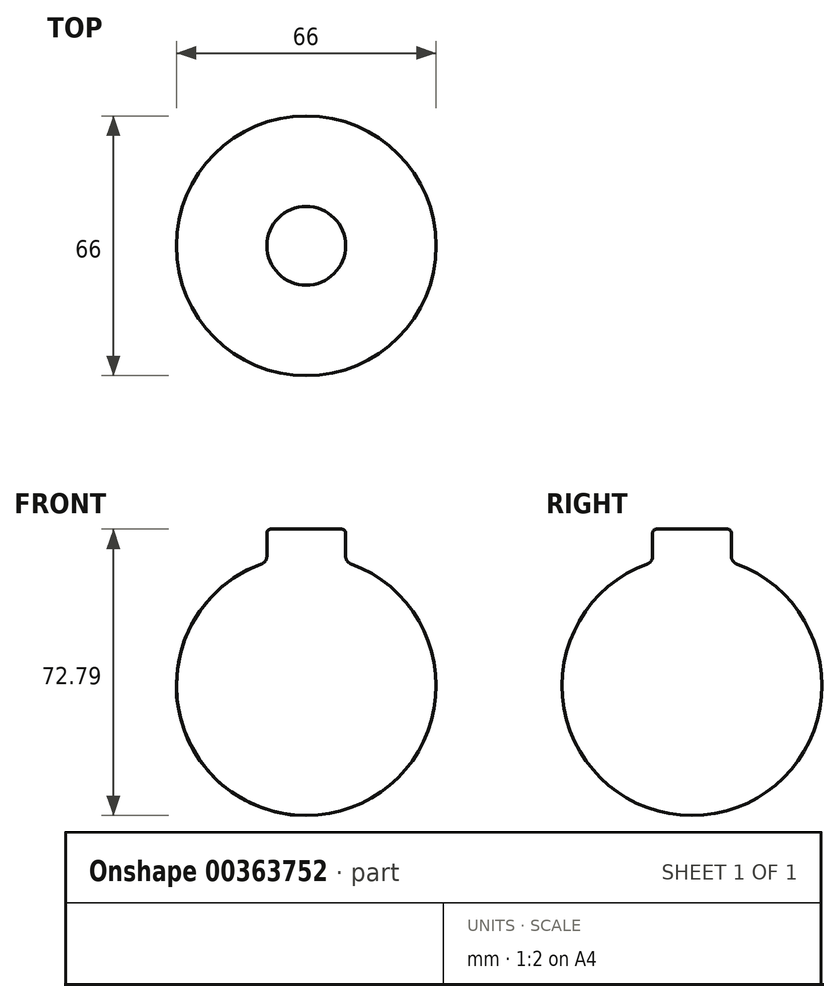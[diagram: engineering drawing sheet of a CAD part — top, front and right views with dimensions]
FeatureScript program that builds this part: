
annotation { "Feature Type Name" : "Feature", "Feature Type Description" : "" }
export const myFeature = defineFeature(function(context is Context, id is Id, definition is map)
    precondition{}
    {
        {
            var Q0;
            Q0=qCreatedBy(makeId("Front.planeOp"),FACE);
            var sketch = newSketch(context, id + "F0", { "sketchPlane" : qUnion([Q0])});
            skCircle(sketch, "E0", {"center": v(0, 0) * mm, "radius": 33 * mm});
            skLineSegment(sketch, "E1", {"start": v(-10, 31.45) * mm, "end": v(-10, 39.79) * mm});
            skLineSegment(sketch, "E2", {"start": v(-10, 39.79) * mm, "end": v(0, 39.79) * mm});
            skLineSegment(sketch, "E3", {"start": v(0, 39.79) * mm, "end": v(10, 39.79) * mm});
            skLineSegment(sketch, "E4", {"start": v(10, 39.79) * mm, "end": v(10, 31.45) * mm});
            skLineSegment(sketch, "E5", {"start": v(0, 39.79) * mm, "end": v(0, -33) * mm});
            skSolve(sketch);
        }
        {
            var Q0;
            {var subQ0=sQuery(id+"F0.wireOp",EDGE,"E0");var subQ1=makeQuery(id+"F0.imprint","INTERSECT",VERTEX,{"derivedFrom":[subQ0,sQuery(id+"F0.wireOp",EDGE,"E1")]});Q0=makeQuery(id+"F0.imprint","IMPRINT",FACE,{"disambiguationData":[TD([[makeQuery(id+"F0.imprint","IMPRINT",EDGE,{"disambiguationData":[TD([[subQ1,1.0]])],"derivedFrom":subQ0}),1.0]])]});}
            var Q1;
            {var subQ0=sQuery(id+"F0.wireOp",EDGE,"E1");Q1=makeQuery(id+"F0.imprint","IMPRINT",FACE,{"disambiguationData":[TD([[makeQuery(id+"F0.imprint","IMPRINT",EDGE,{"derivedFrom":subQ0}),-1.0]])]});}
            var Q2;
            Q2=sQuery(id+"F0.wireOp",EDGE,"E5");
            revolve(context, id + "F1", {"entities" : qUnion([Q0, Q1]), "axis" : qUnion([Q2]), "revolveType" : RevolveType.FULL});
        }
        {
            var Q0;
            Q0=makeQuery(id+"F1.opRevolve","SWEPT_EDGE",EDGE,{"disambiguationData":[OSD([sQuery(id+"F0.wireOp",EDGE,"E1"),sQuery(id+"F0.wireOp",EDGE,"E2")])]});
            fillet(context, id + "F2", {"entities" : qUnion([Q0]), "radius" : 1 * mm, "tangentPropagation" : true, "allowEdgeOverflow" : false});
        }
        {
            var Q0;
            Q0=makeQuery(id+"F1.opRevolve","SWEPT_EDGE",EDGE,{"disambiguationData":[OSD([sQuery(id+"F0.wireOp",EDGE,"E0"),sQuery(id+"F0.wireOp",EDGE,"E1")])]});
            fillet(context, id + "F3", {"entities" : qUnion([Q0]), "radius" : 2 * mm, "tangentPropagation" : true, "allowEdgeOverflow" : false});
        }
    });
